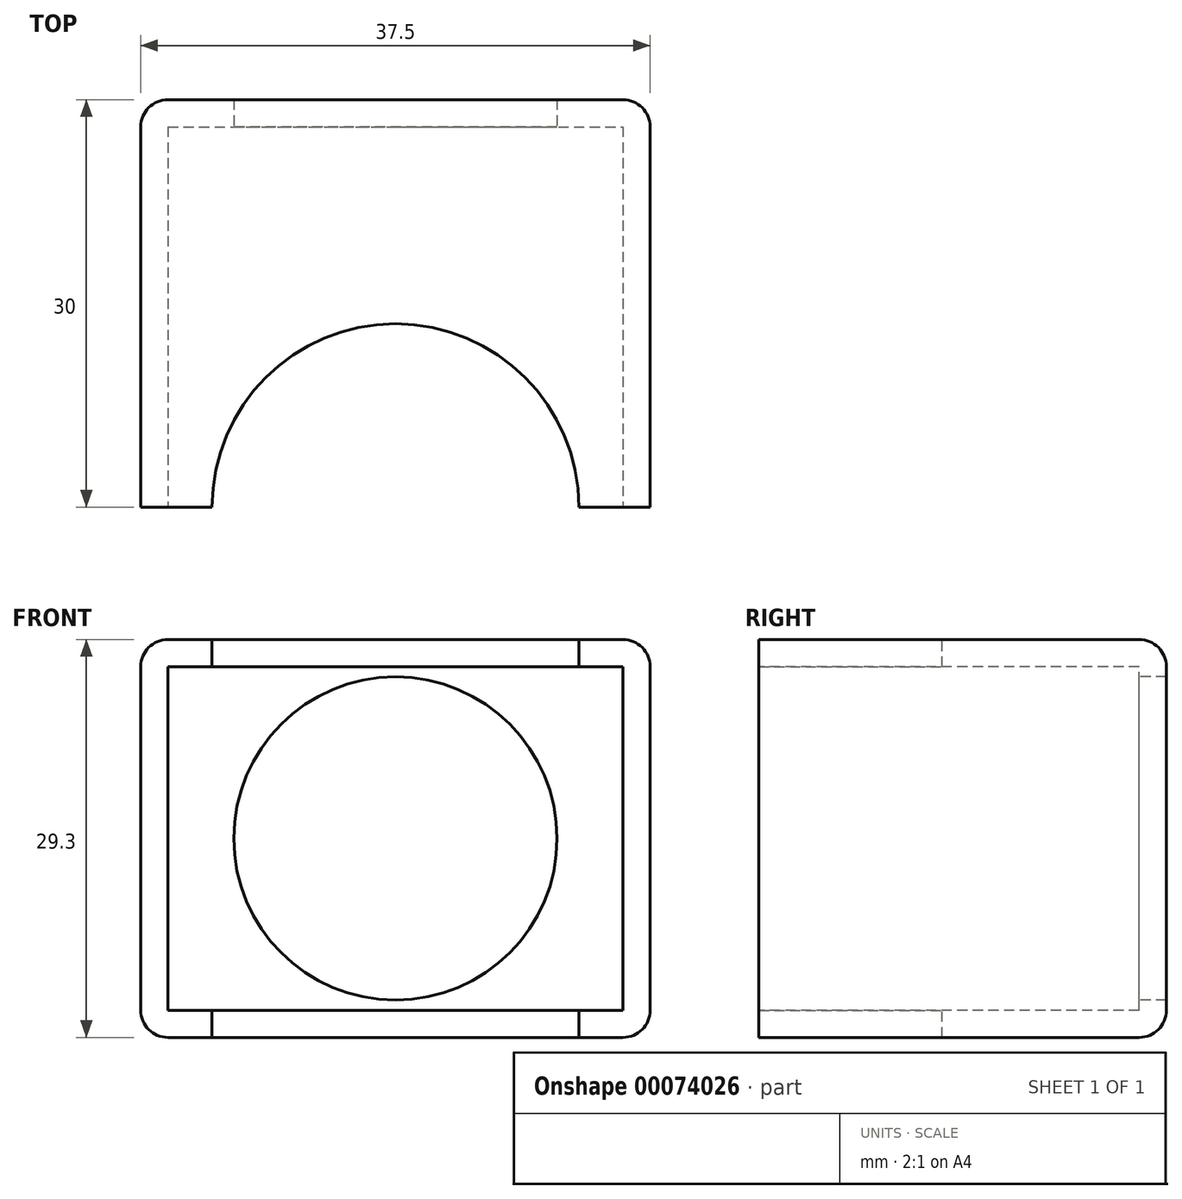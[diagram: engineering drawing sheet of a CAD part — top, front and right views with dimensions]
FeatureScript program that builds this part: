
annotation { "Feature Type Name" : "Feature", "Feature Type Description" : "" }
export const myFeature = defineFeature(function(context is Context, id is Id, definition is map)
    precondition{}
    {
        {
            var Q0;
            Q0=qCreatedBy(makeId("Front.planeOp"),FACE);
            var sketch = newSketch(context, id + "F0", { "sketchPlane" : qUnion([Q0])});
            skLineSegment(sketch, "E0.0", {"start": v(-2.5, 26.8) * mm, "end": v(35, 26.8) * mm});
            skLineSegment(sketch, "E0.1", {"start": v(-2.5, -2.5) * mm, "end": v(-2.5, 26.8) * mm});
            skLineSegment(sketch, "E0.2", {"start": v(-2.5, -2.5) * mm, "end": v(35, -2.5) * mm});
            skLineSegment(sketch, "E0.3", {"start": v(35, -2.5) * mm, "end": v(35, 26.8) * mm});
            skSolve(sketch);
        }
        {
            var Q0;
            Q0=makeQuery(id+"F0.imprint","IMPRINT",FACE,{"disambiguationData":[TD([[makeQuery(id+"F0.imprint","IMPRINT",EDGE,{"derivedFrom":sQuery(id+"F0.wireOp",EDGE,"E0.0")}),-1.0]])]});
            extrude(context, id + "F1", {"entities" : qUnion([Q0]), "depth" : 30 * mm, "offsetDistance" : 25 * mm});
        }
        {
            var Q0;
            Q0=makeQuery(id+"F1.opExtrude","CAP_FACE",FACE,{"disambiguationData":[OSD([sQuery(id+"F0.wireOp",EDGE,"E0.0"),sQuery(id+"F0.wireOp",EDGE,"E0.1"),sQuery(id+"F0.wireOp",EDGE,"E0.2"),sQuery(id+"F0.wireOp",EDGE,"E0.3")])],"isStart":false});
            var sketch = newSketch(context, id + "F2", { "sketchPlane" : qUnion([Q0])});
            skLineSegment(sketch, "E1.0", {"start": v(-0.5, -0.5) * mm, "end": v(-0.5, 24.8) * mm});
            skLineSegment(sketch, "E1.1", {"start": v(-0.5, -0.5) * mm, "end": v(33, -0.5) * mm});
            skLineSegment(sketch, "E1.2", {"start": v(33, -0.5) * mm, "end": v(33, 24.8) * mm});
            skLineSegment(sketch, "E1.3", {"start": v(-0.5, 24.8) * mm, "end": v(33, 24.8) * mm});
            skSolve(sketch);
        }
        {
            var Q0;
            Q0 = qSketchRegion(id + "F2", true);
            extrude(context, id + "F3", {"entities" : qUnion([Q0]), "operationType" : NewBodyOperationType.REMOVE, "oppositeDirection" : true, "depth" : 28 * mm, "offsetDistance" : 25 * mm});
        }
        {
            var Q0;
            Q0=makeQuery(id+"F3.boolean.opBoolean","COPY",FACE,{"derivedFrom":makeQuery(id+"F3.opExtrude","CAP_FACE",FACE,{"disambiguationData":[OSD([sQuery(id+"F2.wireOp",EDGE,"E1.0"),sQuery(id+"F2.wireOp",EDGE,"E1.1"),sQuery(id+"F2.wireOp",EDGE,"E1.2"),sQuery(id+"F2.wireOp",EDGE,"E1.3")])],"isStart":false})});
            var sketch = newSketch(context, id + "F4", { "sketchPlane" : qUnion([Q0])});
            skCircle(sketch, "E2", {"center": v(16.25, 12.15) * mm, "radius": 11.9 * mm});
            skPoint(sketch, "E2.centerSnap0", {"position": v(16.25, -0.5) * mm});
            skPoint(sketch, "E2.centerSnap1", {"position": v(-0.5, 12.15) * mm});
            skSolve(sketch);
        }
        {
            var Q0;
            Q0=makeQuery(id+"F4.imprint","IMPRINT",FACE,{"disambiguationData":[TD([[makeQuery(id+"F4.imprint","IMPRINT",EDGE,{"derivedFrom":sQuery(id+"F4.wireOp",EDGE,"E2")}),1.0]])]});
            extrude(context, id + "F5", {"entities" : qUnion([Q0]), "operationType" : NewBodyOperationType.REMOVE, "endBound" : BoundingType.THROUGH_ALL, "oppositeDirection" : true, "depth" : 25 * mm, "offsetDistance" : 25 * mm});
        }
        {
            var Q0;
            Q0=makeQuery(id+"F1.opExtrude","SWEPT_FACE",FACE,{"disambiguationData":[OSD([sQuery(id+"F0.wireOp",EDGE,"E0.0")])]});
            var sketch = newSketch(context, id + "F6", { "sketchPlane" : qUnion([Q0])});
            skCircle(sketch, "E3", {"center": v(16.25, -30) * mm, "radius": 13.5 * mm});
            skSolve(sketch);
        }
        {
            var Q0;
            {var subQ0=sQuery(id+"F6.wireOp",EDGE,"E3");var subQ1=makeQuery(id+"F1.opExtrude","CAP_EDGE",EDGE,{"disambiguationData":[OSD([sQuery(id+"F0.wireOp",EDGE,"E0.0")])],"isStart":false});var subQ2=makeQuery(id+"F6.imprint","INTERSECT",VERTEX,{"disambiguationData":[OD(0.0)],"derivedFrom":[subQ1,subQ0]});Q0=makeQuery(id+"F6.imprint","IMPRINT",FACE,{"disambiguationData":[TD([[makeQuery(id+"F6.imprint","IMPRINT",EDGE,{"disambiguationData":[TD([[subQ2,1.0]])],"derivedFrom":subQ0}),1.0]])]});}
            extrude(context, id + "F7", {"entities" : qUnion([Q0]), "operationType" : NewBodyOperationType.REMOVE, "endBound" : BoundingType.THROUGH_ALL, "oppositeDirection" : true, "depth" : 25 * mm, "offsetDistance" : 25 * mm});
        }
        {
            var Q0;
            Q0=makeQuery(id+"F1.opExtrude","SWEPT_EDGE",EDGE,{"disambiguationData":[OSD([sQuery(id+"F0.wireOp",EDGE,"E0.0"),sQuery(id+"F0.wireOp",EDGE,"E0.1")])]});
            var Q1;
            Q1=makeQuery(id+"F1.opExtrude","SWEPT_EDGE",EDGE,{"disambiguationData":[OSD([sQuery(id+"F0.wireOp",EDGE,"E0.1"),sQuery(id+"F0.wireOp",EDGE,"E0.2")])]});
            var Q2;
            Q2=makeQuery(id+"F1.opExtrude","SWEPT_EDGE",EDGE,{"disambiguationData":[OSD([sQuery(id+"F0.wireOp",EDGE,"E0.2"),sQuery(id+"F0.wireOp",EDGE,"E0.3")])]});
            var Q3;
            Q3=makeQuery(id+"F1.opExtrude","SWEPT_EDGE",EDGE,{"disambiguationData":[OSD([sQuery(id+"F0.wireOp",EDGE,"E0.0"),sQuery(id+"F0.wireOp",EDGE,"E0.3")])]});
            var Q4;
            Q4=makeQuery(id+"F1.opExtrude","CAP_EDGE",EDGE,{"disambiguationData":[OSD([sQuery(id+"F0.wireOp",EDGE,"E0.0")])],"isStart":true});
            var Q5;
            Q5=makeQuery(id+"F1.opExtrude","CAP_EDGE",EDGE,{"disambiguationData":[OSD([sQuery(id+"F0.wireOp",EDGE,"E0.3")])],"isStart":true});
            var Q6;
            Q6=makeQuery(id+"F1.opExtrude","CAP_EDGE",EDGE,{"disambiguationData":[OSD([sQuery(id+"F0.wireOp",EDGE,"E0.2")])],"isStart":true});
            var Q7;
            Q7=makeQuery(id+"F1.opExtrude","CAP_EDGE",EDGE,{"disambiguationData":[OSD([sQuery(id+"F0.wireOp",EDGE,"E0.1")])],"isStart":true});
            fillet(context, id + "F8", {"entities" : qUnion([Q0, Q1, Q2, Q3, Q4, Q5, Q6, Q7]), "tangentPropagation" : true, "radius" : 2 * mm, "defaultsChanged" : true, "vertexSettings" : [], "allowEdgeOverflow" : false});
        }
    });
